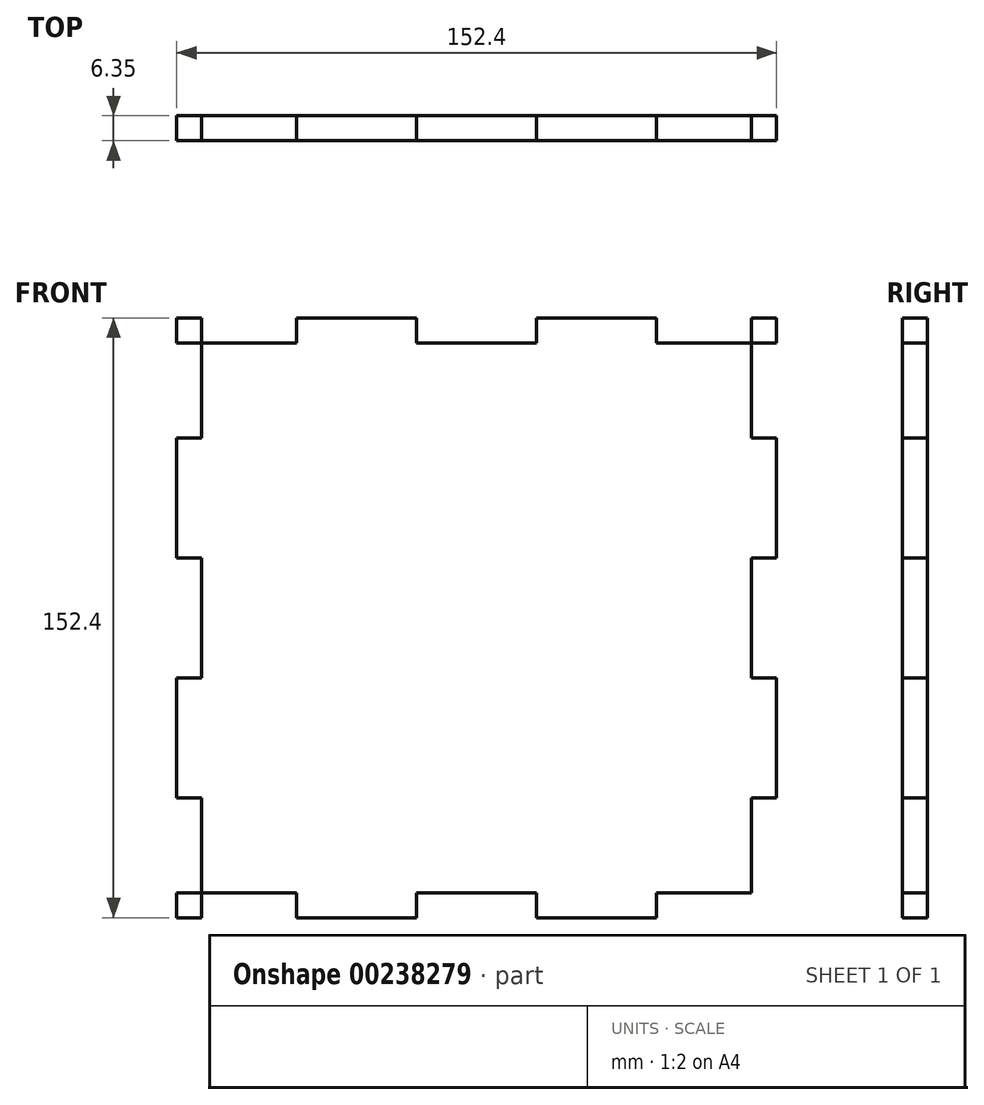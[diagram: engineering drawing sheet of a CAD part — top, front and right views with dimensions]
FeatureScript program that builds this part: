
annotation { "Feature Type Name" : "Feature", "Feature Type Description" : "" }
export const myFeature = defineFeature(function(context is Context, id is Id, definition is map)
    precondition{}
    {
        {
            var Q0;
            Q0=qCreatedBy(makeId("Front.planeOp"),FACE);
            var sketch = newSketch(context, id + "F0", { "sketchPlane" : qUnion([Q0])});
            skLineSegment(sketch, "E0.bottom", {"start": v(76.2, 76.2) * mm, "end": v(-76.2, 76.2) * mm});
            skLineSegment(sketch, "E0.top", {"start": v(76.2, -76.2) * mm, "end": v(-76.2, -76.2) * mm});
            skLineSegment(sketch, "E0.left", {"start": v(76.2, 76.2) * mm, "end": v(76.2, -76.2) * mm});
            skLineSegment(sketch, "E0.right", {"start": v(-76.2, 76.2) * mm, "end": v(-76.2, -76.2) * mm});
            skPoint(sketch, "E0.middle", {"position": v(0, 0) * mm});
            skSolve(sketch);
        }
        {
            var Q0;
            Q0=makeQuery(id+"F0.imprint","IMPRINT",FACE,{"disambiguationData":[TD([[makeQuery(id+"F0.imprint","IMPRINT",EDGE,{"derivedFrom":sQuery(id+"F0.wireOp",EDGE,"E0.bottom")}),1.0]])]});
            extrude(context, id + "F1", {"entities" : qUnion([Q0]), "depth" : 6.35 * mm});
        }
        {
            var Q0;
            Q0=makeQuery(id+"F1.opExtrude","CAP_FACE",FACE,{"disambiguationData":[OSD([sQuery(id+"F0.wireOp",EDGE,"E0.bottom"),sQuery(id+"F0.wireOp",EDGE,"E0.top"),sQuery(id+"F0.wireOp",EDGE,"E0.left"),sQuery(id+"F0.wireOp",EDGE,"E0.right")])],"isStart":false});
            var sketch = newSketch(context, id + "F2", { "sketchPlane" : qUnion([Q0])});
            skLineSegment(sketch, "E1.bottom", {"start": v(-76.2, 76.2) * mm, "end": v(-69.85, 76.2) * mm});
            skLineSegment(sketch, "E1.top", {"start": v(-76.2, 45.72) * mm, "end": v(-69.85, 45.72) * mm});
            skLineSegment(sketch, "E1.left", {"start": v(-76.2, 76.2) * mm, "end": v(-76.2, 45.72) * mm});
            skLineSegment(sketch, "E1.right", {"start": v(-69.85, 76.2) * mm, "end": v(-69.85, 45.72) * mm});
            skLineSegment(sketch, "E2.bottom", {"start": v(-76.2, 15.24) * mm, "end": v(-69.85, 15.24) * mm});
            skLineSegment(sketch, "E2.top", {"start": v(-76.2, -15.24) * mm, "end": v(-69.85, -15.24) * mm});
            skLineSegment(sketch, "E2.left", {"start": v(-76.2, 15.24) * mm, "end": v(-76.2, -15.24) * mm});
            skLineSegment(sketch, "E2.right", {"start": v(-69.85, 15.24) * mm, "end": v(-69.85, -15.24) * mm});
            skLineSegment(sketch, "E3.bottom", {"start": v(-76.2, -76.2) * mm, "end": v(-69.85, -76.2) * mm});
            skLineSegment(sketch, "E3.top", {"start": v(-76.2, -45.72) * mm, "end": v(-69.85, -45.72) * mm});
            skLineSegment(sketch, "E3.left", {"start": v(-76.2, -76.2) * mm, "end": v(-76.2, -45.72) * mm});
            skLineSegment(sketch, "E3.right", {"start": v(-69.85, -76.2) * mm, "end": v(-69.85, -45.72) * mm});
            skLineSegment(sketch, "E4.bottom", {"start": v(-76.2, -76.2) * mm, "end": v(-45.72, -76.2) * mm});
            skLineSegment(sketch, "E4.top", {"start": v(-76.2, -69.85) * mm, "end": v(-45.72, -69.85) * mm});
            skLineSegment(sketch, "E4.left", {"start": v(-76.2, -76.2) * mm, "end": v(-76.2, -69.85) * mm});
            skLineSegment(sketch, "E4.right", {"start": v(-45.72, -76.2) * mm, "end": v(-45.72, -69.85) * mm});
            skLineSegment(sketch, "E5.bottom", {"start": v(-15.24, -76.2) * mm, "end": v(15.24, -76.2) * mm});
            skLineSegment(sketch, "E5.top", {"start": v(-15.24, -69.85) * mm, "end": v(15.24, -69.85) * mm});
            skLineSegment(sketch, "E5.left", {"start": v(-15.24, -76.2) * mm, "end": v(-15.24, -69.85) * mm});
            skLineSegment(sketch, "E5.right", {"start": v(15.24, -76.2) * mm, "end": v(15.24, -69.85) * mm});
            skLineSegment(sketch, "E6.bottom", {"start": v(76.2, -76.2) * mm, "end": v(45.72, -76.2) * mm});
            skLineSegment(sketch, "E6.top", {"start": v(76.2, -69.85) * mm, "end": v(45.72, -69.85) * mm});
            skLineSegment(sketch, "E6.left", {"start": v(76.2, -76.2) * mm, "end": v(76.2, -69.85) * mm});
            skLineSegment(sketch, "E6.right", {"start": v(45.72, -76.2) * mm, "end": v(45.72, -69.85) * mm});
            skLineSegment(sketch, "E7.bottom", {"start": v(76.2, -76.2) * mm, "end": v(69.85, -76.2) * mm});
            skLineSegment(sketch, "E7.top", {"start": v(76.2, -45.72) * mm, "end": v(69.85, -45.72) * mm});
            skLineSegment(sketch, "E7.left", {"start": v(76.2, -76.2) * mm, "end": v(76.2, -45.72) * mm});
            skLineSegment(sketch, "E7.right", {"start": v(69.85, -76.2) * mm, "end": v(69.85, -45.72) * mm});
            skLineSegment(sketch, "E8.bottom", {"start": v(76.2, -15.24) * mm, "end": v(69.85, -15.24) * mm});
            skLineSegment(sketch, "E8.top", {"start": v(76.2, 15.24) * mm, "end": v(69.85, 15.24) * mm});
            skLineSegment(sketch, "E8.left", {"start": v(76.2, -15.24) * mm, "end": v(76.2, 15.24) * mm});
            skLineSegment(sketch, "E8.right", {"start": v(69.85, -15.24) * mm, "end": v(69.85, 15.24) * mm});
            skLineSegment(sketch, "E9.bottom", {"start": v(76.2, 76.2) * mm, "end": v(69.85, 76.2) * mm});
            skLineSegment(sketch, "E9.top", {"start": v(76.2, 45.72) * mm, "end": v(69.85, 45.72) * mm});
            skLineSegment(sketch, "E9.left", {"start": v(76.2, 76.2) * mm, "end": v(76.2, 45.72) * mm});
            skLineSegment(sketch, "E9.right", {"start": v(69.85, 76.2) * mm, "end": v(69.85, 45.72) * mm});
            skLineSegment(sketch, "E10.bottom", {"start": v(-76.2, 76.2) * mm, "end": v(-45.72, 76.2) * mm});
            skLineSegment(sketch, "E10.top", {"start": v(-76.2, 69.85) * mm, "end": v(-45.72, 69.85) * mm});
            skLineSegment(sketch, "E10.left", {"start": v(-76.2, 76.2) * mm, "end": v(-76.2, 69.85) * mm});
            skLineSegment(sketch, "E10.right", {"start": v(-45.72, 76.2) * mm, "end": v(-45.72, 69.85) * mm});
            skLineSegment(sketch, "E11.bottom", {"start": v(-15.24, 76.2) * mm, "end": v(15.24, 76.2) * mm});
            skLineSegment(sketch, "E11.top", {"start": v(-15.24, 69.85) * mm, "end": v(15.24, 69.85) * mm});
            skLineSegment(sketch, "E11.left", {"start": v(-15.24, 76.2) * mm, "end": v(-15.24, 69.85) * mm});
            skLineSegment(sketch, "E11.right", {"start": v(15.24, 76.2) * mm, "end": v(15.24, 69.85) * mm});
            skLineSegment(sketch, "E12.bottom", {"start": v(76.2, 76.2) * mm, "end": v(45.72, 76.2) * mm});
            skLineSegment(sketch, "E12.top", {"start": v(76.2, 69.85) * mm, "end": v(45.72, 69.85) * mm});
            skLineSegment(sketch, "E12.left", {"start": v(76.2, 76.2) * mm, "end": v(76.2, 69.85) * mm});
            skLineSegment(sketch, "E12.right", {"start": v(45.72, 76.2) * mm, "end": v(45.72, 69.85) * mm});
            skSolve(sketch);
        }
        {
            var Q0;
            {var subQ5=sQuery(id+"F2.wireOp",EDGE,"E10.right");Q0=makeQuery(id+"F2.imprint","IMPRINT",FACE,{"disambiguationData":[TD([[makeQuery(id+"F2.imprint","IMPRINT",EDGE,{"derivedFrom":subQ5}),-1.0]])]});}
            var Q1;
            {var subQ5=sQuery(id+"F2.wireOp",EDGE,"E10.left");Q1=makeQuery(id+"F2.imprint","IMPRINT",FACE,{"disambiguationData":[TD([[makeQuery(id+"F2.imprint","IMPRINT",EDGE,{"derivedFrom":subQ5}),1.0]])]});}
            var Q2;
            {var subQ0=sQuery(id+"F2.wireOp",EDGE,"E1.top");Q2=makeQuery(id+"F2.imprint","IMPRINT",FACE,{"disambiguationData":[TD([[makeQuery(id+"F2.imprint","IMPRINT",EDGE,{"derivedFrom":subQ0}),1.0]])]});}
            var Q3;
            Q3=makeQuery(id+"F2.imprint","IMPRINT",FACE,{"disambiguationData":[TD([[makeQuery(id+"F2.imprint","IMPRINT",EDGE,{"derivedFrom":sQuery(id+"F2.wireOp",EDGE,"E2.bottom")}),-1.0]])]});
            var Q4;
            {var subQ0=sQuery(id+"F2.wireOp",EDGE,"E3.top");Q4=makeQuery(id+"F2.imprint","IMPRINT",FACE,{"disambiguationData":[TD([[makeQuery(id+"F2.imprint","IMPRINT",EDGE,{"derivedFrom":subQ0}),-1.0]])]});}
            var Q5;
            {var subQ5=sQuery(id+"F2.wireOp",EDGE,"E4.left");Q5=makeQuery(id+"F2.imprint","IMPRINT",FACE,{"disambiguationData":[TD([[makeQuery(id+"F2.imprint","IMPRINT",EDGE,{"derivedFrom":subQ5}),1.0]])]});}
            var Q6;
            {var subQ5=sQuery(id+"F2.wireOp",EDGE,"E4.right");Q6=makeQuery(id+"F2.imprint","IMPRINT",FACE,{"disambiguationData":[TD([[makeQuery(id+"F2.imprint","IMPRINT",EDGE,{"derivedFrom":subQ5}),1.0]])]});}
            var Q7;
            Q7=makeQuery(id+"F2.imprint","IMPRINT",FACE,{"disambiguationData":[TD([[makeQuery(id+"F2.imprint","IMPRINT",EDGE,{"derivedFrom":sQuery(id+"F2.wireOp",EDGE,"E5.bottom")}),-1.0]])]});
            var Q8;
            {var subQ0=sQuery(id+"F2.wireOp",EDGE,"E6.bottom");Q8=makeQuery(id+"F2.imprint","IMPRINT",FACE,{"disambiguationData":[TD([[makeQuery(id+"F2.imprint","IMPRINT",EDGE,{"derivedFrom":subQ0}),-1.0]])]});}
            var Q9;
            {var subQ5=sQuery(id+"F2.wireOp",EDGE,"E7.bottom");Q9=makeQuery(id+"F2.imprint","IMPRINT",FACE,{"disambiguationData":[TD([[makeQuery(id+"F2.imprint","IMPRINT",EDGE,{"derivedFrom":subQ5}),-1.0]])]});}
            var Q10;
            {var subQ5=sQuery(id+"F2.wireOp",EDGE,"E7.top");Q10=makeQuery(id+"F2.imprint","IMPRINT",FACE,{"disambiguationData":[TD([[makeQuery(id+"F2.imprint","IMPRINT",EDGE,{"derivedFrom":subQ5}),1.0]])]});}
            var Q11;
            Q11=makeQuery(id+"F2.imprint","IMPRINT",FACE,{"disambiguationData":[TD([[makeQuery(id+"F2.imprint","IMPRINT",EDGE,{"derivedFrom":sQuery(id+"F2.wireOp",EDGE,"E8.bottom")}),-1.0]])]});
            var Q12;
            {var subQ0=sQuery(id+"F2.wireOp",EDGE,"E9.top");Q12=makeQuery(id+"F2.imprint","IMPRINT",FACE,{"disambiguationData":[TD([[makeQuery(id+"F2.imprint","IMPRINT",EDGE,{"derivedFrom":subQ0}),-1.0]])]});}
            var Q13;
            {var subQ5=sQuery(id+"F2.wireOp",EDGE,"E12.left");Q13=makeQuery(id+"F2.imprint","IMPRINT",FACE,{"disambiguationData":[TD([[makeQuery(id+"F2.imprint","IMPRINT",EDGE,{"derivedFrom":subQ5}),-1.0]])]});}
            var Q14;
            {var subQ5=sQuery(id+"F2.wireOp",EDGE,"E12.right");Q14=makeQuery(id+"F2.imprint","IMPRINT",FACE,{"disambiguationData":[TD([[makeQuery(id+"F2.imprint","IMPRINT",EDGE,{"derivedFrom":subQ5}),1.0]])]});}
            var Q15;
            Q15=makeQuery(id+"F2.imprint","IMPRINT",FACE,{"disambiguationData":[TD([[makeQuery(id+"F2.imprint","IMPRINT",EDGE,{"derivedFrom":sQuery(id+"F2.wireOp",EDGE,"E11.bottom")}),1.0]])]});
            extrude(context, id + "F3", {"entities" : qUnion([Q0, Q1, Q2, Q3, Q4, Q5, Q6, Q7, Q8, Q9, Q10, Q11, Q12, Q13, Q14, Q15]), "operationType" : NewBodyOperationType.REMOVE, "endBound" : BoundingType.THROUGH_ALL, "oppositeDirection" : true, "depth" : 25.4 * mm});
        }
    });
